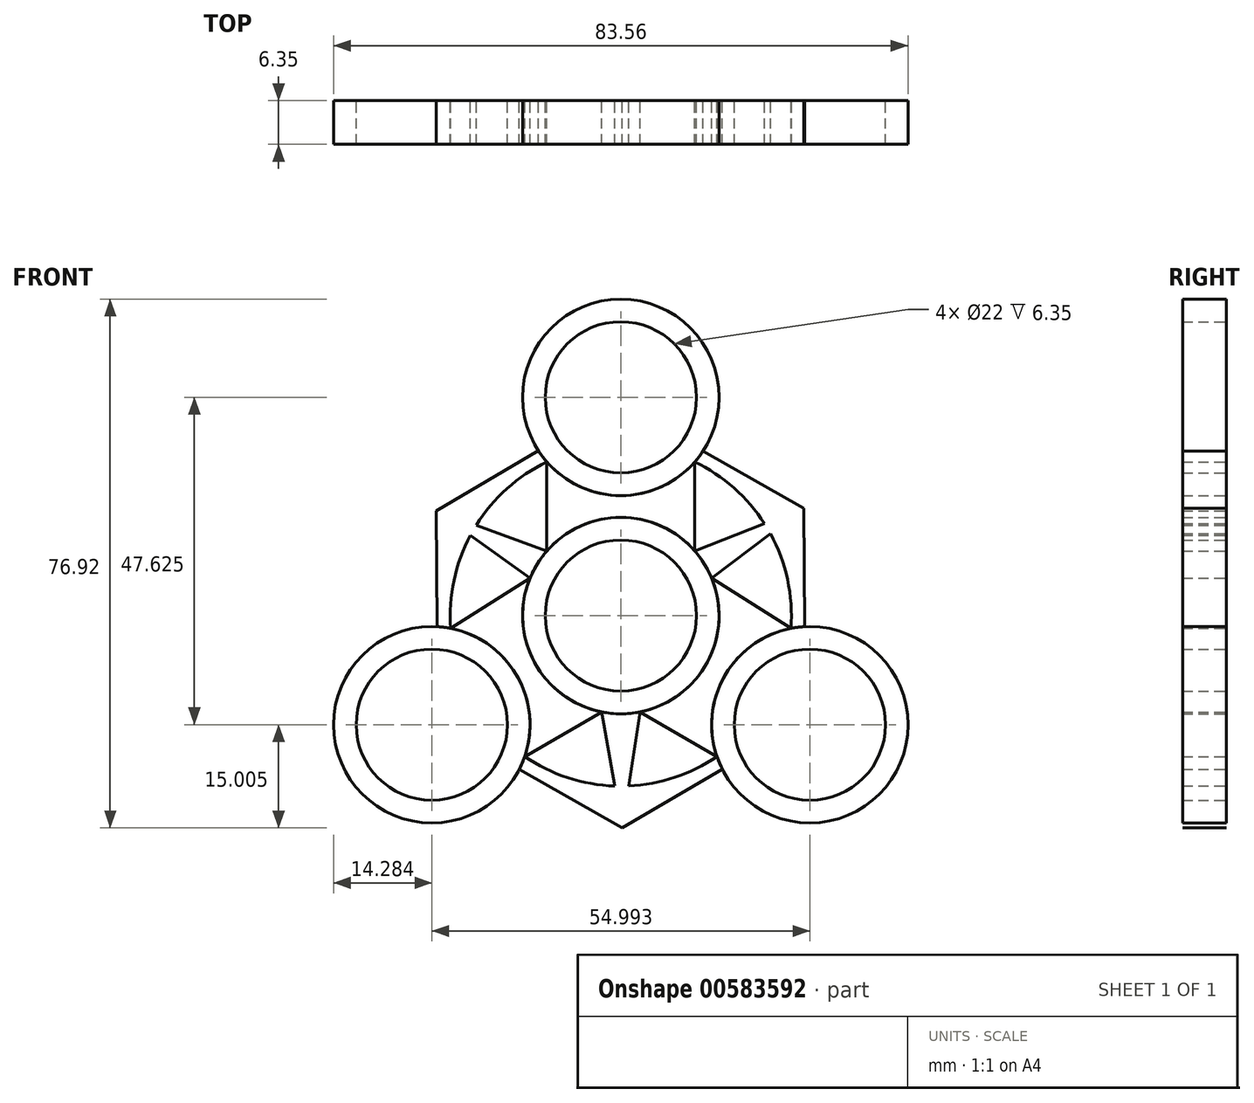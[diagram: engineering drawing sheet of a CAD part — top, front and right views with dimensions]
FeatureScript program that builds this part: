
annotation { "Feature Type Name" : "Feature", "Feature Type Description" : "" }
export const myFeature = defineFeature(function(context is Context, id is Id, definition is map)
    precondition{}
    {
        {
            var Q0;
            Q0=qCreatedBy(makeId("Front.planeOp"),FACE);
            var sketch = newSketch(context, id + "F0", { "sketchPlane" : qUnion([Q0])});
            skCircle(sketch, "E0", {"center": v(0, 0) * mm, "radius": 14.29 * mm});
            skCircle(sketch, "E1", {"center": v(0, 0) * mm, "radius": 11 * mm});
            skCircle(sketch, "E2", {"center": v(0, 31.75) * mm, "radius": 14.29 * mm});
            skCircle(sketch, "E3", {"center": v(0, 31.75) * mm, "radius": 11 * mm});
            skCircle(sketch, "E4.1.0", {"center": v(-27.5, -15.87) * mm, "radius": 11 * mm});
            skCircle(sketch, "E4.1.1", {"center": v(-27.5, -15.87) * mm, "radius": 14.29 * mm});
            skCircle(sketch, "E4.2.0", {"center": v(27.5, -15.88) * mm, "radius": 11 * mm});
            skCircle(sketch, "E4.2.1", {"center": v(27.5, -15.88) * mm, "radius": 14.29 * mm});
            skSolve(sketch);
        }
        {
            var Q0;
            Q0=qCreatedBy(makeId("Front.planeOp"),FACE);
            var sketch = newSketch(context, id + "F1", { "sketchPlane" : qUnion([Q0])});
            skCircle(sketch, "E5.0", {"center": v(0, 31.75) * mm, "radius": 14.29 * mm});
            skCircle(sketch, "E6.0", {"center": v(0, 0) * mm, "radius": 14.29 * mm});
            skCircle(sketch, "E7.0", {"center": v(-27.5, -15.87) * mm, "radius": 14.29 * mm});
            skCircle(sketch, "E8.0", {"center": v(27.5, -15.88) * mm, "radius": 14.29 * mm});
            skArc(sketch, "E9", {"start": v(-10.76, 22.35) * mm, "mid": v(-21.49, 12.4) * mm, "end": v(-24.74, -1.86) * mm});
            skArc(sketch, "E10.trimOffspring", {"start": v(24.74, -1.86) * mm, "mid": v(21.49, 12.4) * mm, "end": v(10.76, 22.35) * mm});
            skArc(sketch, "E11.trimOffspring", {"start": v(-13.98, -20.5) * mm, "mid": v(0, -24.8) * mm, "end": v(13.98, -20.5) * mm});
            skLineSegment(sketch, "E12", {"start": v(-10.76, 22.35) * mm, "end": v(-10.76, 9.4) * mm});
            skLineSegment(sketch, "E13", {"start": v(10.76, 22.35) * mm, "end": v(10.76, 9.4) * mm});
            skLineSegment(sketch, "E14", {"start": v(-24.74, -1.86) * mm, "end": v(-13.21, 5.44) * mm});
            skLineSegment(sketch, "E15", {"start": v(24.74, -1.86) * mm, "end": v(13.21, 5.44) * mm});
            skArc(sketch, "E16.cCircle", {"start": v(-11.95, 23.92) * mm, "mid": v(-12.75, 23.5) * mm, "end": v(-13.53, 23.07) * mm, "construction": true});
            skLineSegment(sketch, "E16.0", {"start": v(0.21, -30.88) * mm, "end": v(-14.77, -22.37) * mm});
            skLineSegment(sketch, "E16.1", {"start": v(-26.73, -1.6) * mm, "end": v(-26.85, 15.26) * mm});
            skLineSegment(sketch, "E16.2", {"start": v(-26.85, 15.26) * mm, "end": v(-11.99, 23.97) * mm});
            skLineSegment(sketch, "E16.3", {"start": v(11.97, 23.96) * mm, "end": v(26.64, 15.63) * mm});
            skLineSegment(sketch, "E16.4", {"start": v(26.64, 15.63) * mm, "end": v(26.76, -1.6) * mm});
            skLineSegment(sketch, "E16.5", {"start": v(14.76, -22.35) * mm, "end": v(0.21, -30.88) * mm});
            skPoint(sketch, "E16.0.midPoint", {"position": v(-13.21, -23.25) * mm});
            skArc(sketch, "E17.trimOffspring", {"start": v(13.21, 23.25) * mm, "mid": v(12.59, 23.6) * mm, "end": v(11.95, 23.92) * mm, "construction": true});
            skArc(sketch, "E18.trimOffspring", {"start": v(26.7, -1.6) * mm, "mid": v(26.73, -0.71) * mm, "end": v(26.74, 0.19) * mm, "construction": true});
            skArc(sketch, "E19.trimOffspring", {"start": v(13.53, -23.07) * mm, "mid": v(14.14, -22.7) * mm, "end": v(14.74, -22.31) * mm, "construction": true});
            skArc(sketch, "E20.trimOffspring", {"start": v(-14.74, -22.31) * mm, "mid": v(-13.98, -22.8) * mm, "end": v(-13.21, -23.25) * mm, "construction": true});
            skArc(sketch, "E21.trimOffspring", {"start": v(-26.74, -0.19) * mm, "mid": v(-26.73, -0.9) * mm, "end": v(-26.7, -1.6) * mm, "construction": true});
            skPoint(sketch, "E22.orphan", {"position": v(-26.64, -15.63) * mm});
            skPoint(sketch, "E23.orphan", {"position": v(26.85, -15.26) * mm});
            skPoint(sketch, "E24.orphan", {"position": v(-0.21, 30.88) * mm});
            skLineSegment(sketch, "E25", {"start": v(-21.04, 13.14) * mm, "end": v(-10.76, 9.4) * mm});
            skLineSegment(sketch, "E26", {"start": v(-21.89, 11.68) * mm, "end": v(-13.21, 5.44) * mm});
            skLineSegment(sketch, "E27", {"start": v(20.9, 13.37) * mm, "end": v(10.76, 9.4) * mm});
            skLineSegment(sketch, "E28", {"start": v(13.21, 5.44) * mm, "end": v(21.76, 11.92) * mm});
            skLineSegment(sketch, "E29", {"start": v(-13.98, -20.5) * mm, "end": v(-2.78, -14.01) * mm});
            skLineSegment(sketch, "E30", {"start": v(2.78, -14.01) * mm, "end": v(13.98, -20.5) * mm});
            skLineSegment(sketch, "E31", {"start": v(2.78, -14.01) * mm, "end": v(1.14, -24.78) * mm});
            skLineSegment(sketch, "E32", {"start": v(-2.78, -14.01) * mm, "end": v(-0.87, -24.8) * mm});
            skSolve(sketch);
        }
        {
            var Q0;
            Q0=makeQuery(id+"F0.imprint","IMPRINT",FACE,{"disambiguationData":[TD([[makeQuery(id+"F0.imprint","IMPRINT",EDGE,{"derivedFrom":sQuery(id+"F0.wireOp",EDGE,"E4.2.0")}),-1.0]])]});
            var Q1;
            Q1=makeQuery(id+"F0.imprint","IMPRINT",FACE,{"disambiguationData":[TD([[makeQuery(id+"F0.imprint","IMPRINT",EDGE,{"derivedFrom":sQuery(id+"F0.wireOp",EDGE,"E0")}),1.0]])]});
            var Q2;
            Q2=makeQuery(id+"F0.imprint","IMPRINT",FACE,{"disambiguationData":[TD([[makeQuery(id+"F0.imprint","IMPRINT",EDGE,{"derivedFrom":sQuery(id+"F0.wireOp",EDGE,"E2")}),1.0]])]});
            var Q3;
            Q3=makeQuery(id+"F0.imprint","IMPRINT",FACE,{"disambiguationData":[TD([[makeQuery(id+"F0.imprint","IMPRINT",EDGE,{"derivedFrom":sQuery(id+"F0.wireOp",EDGE,"E4.1.0")}),-1.0]])]});
            var Q4;
            {var subQ0=sQuery(id+"F1.wireOp",EDGE,"E15");Q4=makeQuery(id+"F1.imprint","IMPRINT",FACE,{"disambiguationData":[TD([[makeQuery(id+"F1.imprint","IMPRINT",EDGE,{"derivedFrom":subQ0}),1.0]])]});}
            var Q5;
            {var subQ0=sQuery(id+"F1.wireOp",EDGE,"E12");Q5=makeQuery(id+"F1.imprint","IMPRINT",FACE,{"disambiguationData":[TD([[makeQuery(id+"F1.imprint","IMPRINT",EDGE,{"derivedFrom":subQ0}),1.0]])]});}
            var Q6;
            {var subQ0=sQuery(id+"F1.wireOp",EDGE,"E14");Q6=makeQuery(id+"F1.imprint","IMPRINT",FACE,{"disambiguationData":[TD([[makeQuery(id+"F1.imprint","IMPRINT",EDGE,{"derivedFrom":subQ0}),-1.0]])]});}
            var Q7;
            {var subQ2=sQuery(id+"F1.wireOp",EDGE,"E31");Q7=makeQuery(id+"F1.imprint","IMPRINT",FACE,{"disambiguationData":[TD([[makeQuery(id+"F1.imprint","IMPRINT",EDGE,{"derivedFrom":subQ2}),-1.0]])]});}
            var Q8;
            {var subQ0=sQuery(id+"F1.wireOp",EDGE,"E27");Q8=makeQuery(id+"F1.imprint","IMPRINT",FACE,{"disambiguationData":[TD([[makeQuery(id+"F1.imprint","IMPRINT",EDGE,{"derivedFrom":subQ0}),1.0]])]});}
            var Q9;
            {var subQ0=sQuery(id+"F1.wireOp",EDGE,"E25");Q9=makeQuery(id+"F1.imprint","IMPRINT",FACE,{"disambiguationData":[TD([[makeQuery(id+"F1.imprint","IMPRINT",EDGE,{"derivedFrom":subQ0}),-1.0]])]});}
            var Q10;
            {var subQ7=sQuery(id+"F1.wireOp",EDGE,"E16.1");Q10=makeQuery(id+"F1.imprint","IMPRINT",FACE,{"disambiguationData":[TD([[makeQuery(id+"F1.imprint","IMPRINT",EDGE,{"derivedFrom":subQ7}),-1.0]])]});}
            var Q11;
            {var subQ8=sQuery(id+"F1.wireOp",EDGE,"E16.3");Q11=makeQuery(id+"F1.imprint","IMPRINT",FACE,{"disambiguationData":[TD([[makeQuery(id+"F1.imprint","IMPRINT",EDGE,{"derivedFrom":subQ8}),-1.0]])]});}
            var Q12;
            {var subQ8=sQuery(id+"F1.wireOp",EDGE,"E16.0");Q12=makeQuery(id+"F1.imprint","IMPRINT",FACE,{"disambiguationData":[TD([[makeQuery(id+"F1.imprint","IMPRINT",EDGE,{"derivedFrom":subQ8}),-1.0]])]});}
            extrude(context, id + "F2", {"entities" : qUnion([Q0, Q1, Q2, Q3, Q4, Q5, Q6, Q7, Q8, Q9, Q10, Q11, Q12]), "depth" : 6.35 * mm, "offsetDistance" : 25.4 * mm});
        }
    });
